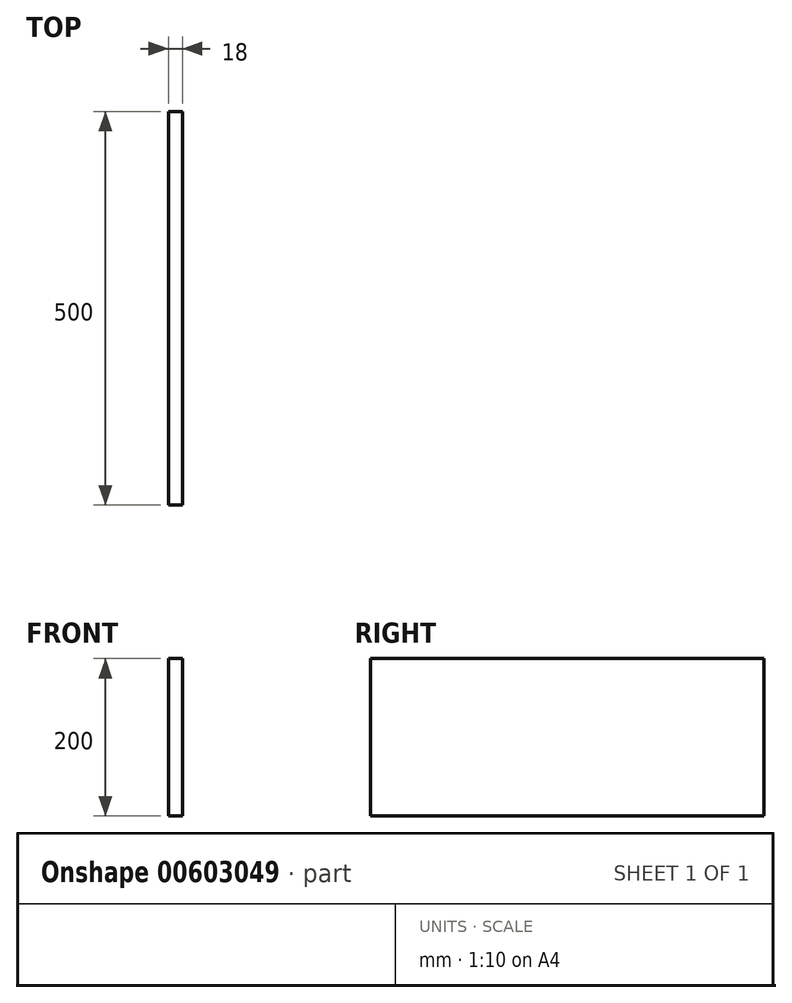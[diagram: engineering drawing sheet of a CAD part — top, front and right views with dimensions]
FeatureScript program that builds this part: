
annotation { "Feature Type Name" : "Feature", "Feature Type Description" : "" }
export const myFeature = defineFeature(function(context is Context, id is Id, definition is map)
    precondition{}
    {
        {
            var Q0;
            Q0=qCreatedBy(makeId("Right.planeOp"),FACE);
            var sketch = newSketch(context, id + "F0", { "sketchPlane" : qUnion([Q0])});
            skLineSegment(sketch, "E0.bottom", {"start": v(0, 0) * mm, "end": v(-500, 0) * mm});
            skLineSegment(sketch, "E0.top", {"start": v(0, 200) * mm, "end": v(-500, 200) * mm});
            skLineSegment(sketch, "E0.left", {"start": v(0, 0) * mm, "end": v(0, 200) * mm});
            skLineSegment(sketch, "E0.right", {"start": v(-500, 0) * mm, "end": v(-500, 200) * mm});
            skSolve(sketch);
        }
        {
            var Q0;
            Q0=makeQuery(id+"F0.imprint","IMPRINT",FACE,{"disambiguationData":[TD([[makeQuery(id+"F0.imprint","IMPRINT",EDGE,{"derivedFrom":sQuery(id+"F0.wireOp",EDGE,"E0.bottom")}),-1.0]])]});
            var Q1;
            Q1=sQuery(id+"F0.wireOp",EDGE,"E0.bottom");
            extrude(context, id + "F1", {"entities" : qUnion([Q0]), "surfaceEntities" : qUnion([Q1]), "depth" : 18 * mm, "offsetDistance" : 25 * mm});
        }
    });
